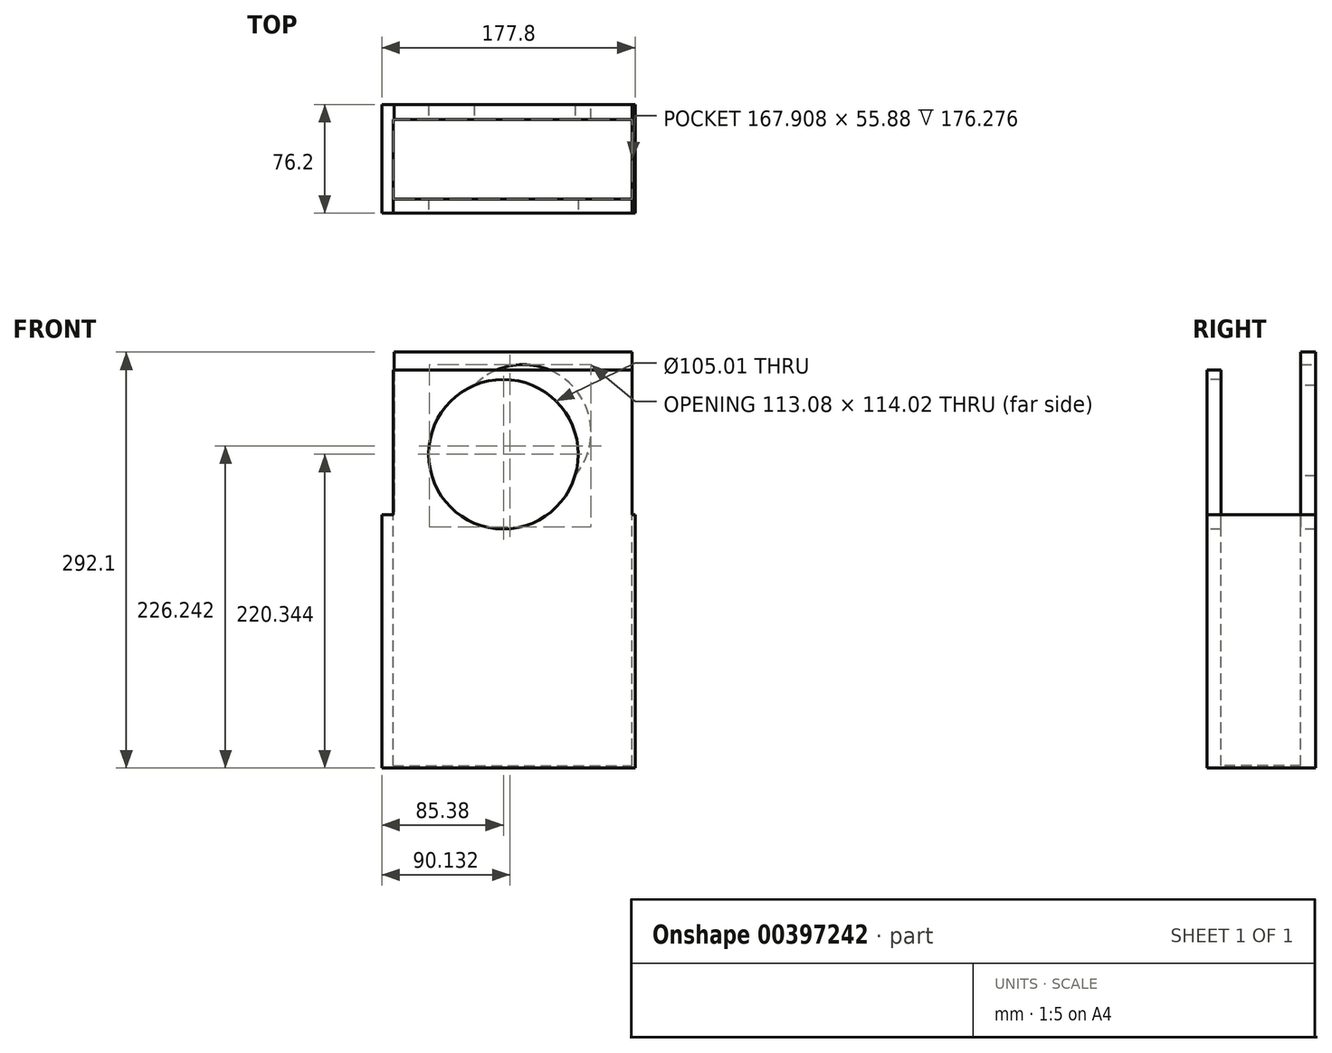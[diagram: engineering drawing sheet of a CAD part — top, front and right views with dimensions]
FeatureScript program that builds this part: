
annotation { "Feature Type Name" : "Feature", "Feature Type Description" : "" }
export const myFeature = defineFeature(function(context is Context, id is Id, definition is map)
    precondition{}
    {
        {
            var Q0;
            Q0=qCreatedBy(makeId("Front.planeOp"),FACE);
            var sketch = newSketch(context, id + "F0", { "sketchPlane" : qUnion([Q0])});
            skLineSegment(sketch, "E0.bottom", {"start": v(-137.9, 76.57) * mm, "end": v(39.9, 76.57) * mm});
            skLineSegment(sketch, "E0.top", {"start": v(-137.9, -101.23) * mm, "end": v(39.9, -101.23) * mm});
            skLineSegment(sketch, "E0.left", {"start": v(-137.9, 76.57) * mm, "end": v(-137.9, -101.23) * mm});
            skLineSegment(sketch, "E0.right", {"start": v(39.9, 76.57) * mm, "end": v(39.9, -101.23) * mm});
            skSolve(sketch);
        }
        {
            var Q0;
            Q0 = qSketchRegion(id + "F0", true);
            extrude(context, id + "F1", {"entities" : qUnion([Q0]), "depth" : 76.2 * mm});
        }
        {
            var Q0;
            Q0=makeQuery(id+"F1.opExtrude","SWEPT_FACE",FACE,{"disambiguationData":[OSD([sQuery(id+"F0.wireOp",EDGE,"E0.bottom")])]});
            var sketch = newSketch(context, id + "F2", { "sketchPlane" : qUnion([Q0])});
            skLineSegment(sketch, "E1.bottom", {"start": v(-129.97, -10.44) * mm, "end": v(37.94, -10.44) * mm});
            skLineSegment(sketch, "E1.top", {"start": v(-129.97, -66.32) * mm, "end": v(37.94, -66.32) * mm});
            skLineSegment(sketch, "E1.left", {"start": v(-129.97, -10.44) * mm, "end": v(-129.97, -66.32) * mm});
            skLineSegment(sketch, "E1.right", {"start": v(37.94, -10.44) * mm, "end": v(37.94, -66.32) * mm});
            skSolve(sketch);
        }
        {
            var Q0;
            Q0 = qSketchRegion(id + "F2", true);
            extrude(context, id + "F3", {"entities" : qUnion([Q0]), "operationType" : NewBodyOperationType.REMOVE, "oppositeDirection" : true, "depth" : 176.28 * mm});
        }
        {
            var Q0;
            Q0=makeQuery(id+"F1.opExtrude","SWEPT_FACE",FACE,{"disambiguationData":[OSD([sQuery(id+"F0.wireOp",EDGE,"E0.bottom")])]});
            var sketch = newSketch(context, id + "F4", { "sketchPlane" : qUnion([Q0])});
            skLineSegment(sketch, "E2.bottom", {"start": v(-129.97, -66.32) * mm, "end": v(37.94, -66.32) * mm});
            skLineSegment(sketch, "E2.top", {"start": v(-129.97, -76.2) * mm, "end": v(37.94, -76.2) * mm});
            skLineSegment(sketch, "E2.left", {"start": v(-129.97, -66.32) * mm, "end": v(-129.97, -76.2) * mm});
            skLineSegment(sketch, "E2.right", {"start": v(37.94, -66.32) * mm, "end": v(37.94, -76.2) * mm});
            skSolve(sketch);
        }
        {
            var Q0;
            Q0 = qSketchRegion(id + "F4", true);
            extrude(context, id + "F5", {"entities" : qUnion([Q0]), "operationType" : NewBodyOperationType.ADD, "depth" : 101.6 * mm});
        }
        {
            var Q0;
            Q0=makeQuery(id+"F1.opExtrude","SWEPT_FACE",FACE,{"disambiguationData":[OSD([sQuery(id+"F0.wireOp",EDGE,"E0.bottom")])]});
            var sketch = newSketch(context, id + "F6", { "sketchPlane" : qUnion([Q0])});
            skLineSegment(sketch, "E3.bottom", {"start": v(37.94, -10.44) * mm, "end": v(-129.28, -10.44) * mm});
            skLineSegment(sketch, "E3.top", {"start": v(37.94, 0) * mm, "end": v(-129.28, 0) * mm});
            skLineSegment(sketch, "E3.left", {"start": v(37.94, -10.44) * mm, "end": v(37.94, 0) * mm});
            skLineSegment(sketch, "E3.right", {"start": v(-129.28, -10.44) * mm, "end": v(-129.28, 0) * mm});
            skSolve(sketch);
        }
        {
            var Q0;
            Q0 = qSketchRegion(id + "F6", true);
            extrude(context, id + "F7", {"entities" : qUnion([Q0]), "operationType" : NewBodyOperationType.ADD, "depth" : 114.3 * mm});
        }
        {
            var Q0;
            Q0=makeQuery(id+"F7.boolean.opBoolean","MERGE",FACE,{"derivedFrom":[makeQuery(id+"F1.opExtrude","CAP_FACE",FACE,{"disambiguationData":[OSD([sQuery(id+"F0.wireOp",EDGE,"E0.bottom"),sQuery(id+"F0.wireOp",EDGE,"E0.top"),sQuery(id+"F0.wireOp",EDGE,"E0.left"),sQuery(id+"F0.wireOp",EDGE,"E0.right")])],"isStart":true}),makeQuery(id+"F7.opExtrude","SWEPT_FACE",FACE,{"disambiguationData":[OSD([sQuery(id+"F6.wireOp",EDGE,"E3.top")])]})]});
            var sketch = newSketch(context, id + "F8", { "sketchPlane" : qUnion([Q0])});
            skCircle(sketch, "E4", {"center": v(38.71, 134.44) * mm, "radius": 47.6 * mm});
            skSolve(sketch);
        }
        {
            var Q0;
            Q0 = qSketchRegion(id + "F8", true);
            extrude(context, id + "F9", {"entities" : qUnion([Q0]), "operationType" : NewBodyOperationType.REMOVE, "oppositeDirection" : true, "depth" : 41.9 * mm});
        }
        {
            var Q0;
            Q0=makeQuery(id+"F5.boolean.opBoolean","MERGE",FACE,{"derivedFrom":[makeQuery(id+"F1.opExtrude","CAP_FACE",FACE,{"disambiguationData":[OSD([sQuery(id+"F0.wireOp",EDGE,"E0.bottom"),sQuery(id+"F0.wireOp",EDGE,"E0.top"),sQuery(id+"F0.wireOp",EDGE,"E0.left"),sQuery(id+"F0.wireOp",EDGE,"E0.right")])],"isStart":false}),makeQuery(id+"F5.opExtrude","SWEPT_FACE",FACE,{"disambiguationData":[OSD([sQuery(id+"F4.wireOp",EDGE,"E2.top")])]})]});
            var sketch = newSketch(context, id + "F10", { "sketchPlane" : qUnion([Q0])});
            skCircle(sketch, "E5", {"center": v(-52.5, 119.11) * mm, "radius": 52.5 * mm});
            skSolve(sketch);
        }
        {
            var Q0;
            Q0 = qSketchRegion(id + "F10", true);
            extrude(context, id + "F11", {"entities" : qUnion([Q0]), "operationType" : NewBodyOperationType.REMOVE, "oppositeDirection" : true, "depth" : 159 * mm});
        }
    });
